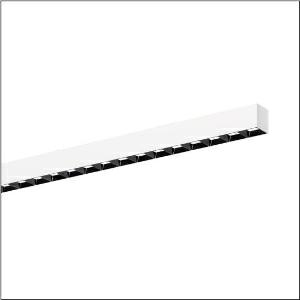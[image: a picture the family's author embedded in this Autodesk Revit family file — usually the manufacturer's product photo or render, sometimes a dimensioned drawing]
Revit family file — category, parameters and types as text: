
# Revit family: silica_r__21_51mx22da34wb_da43
name_source: partatom
category: Lighting Fixtures
units: mm (PartAtom-declared; Revit-internal decimal feet)

## family parameters
Cut with Voids When Loaded = No
Host = Face
Light Source = No
Part Type = Normal
Room Calculation Point = No
Round Connector Dimension = Use Diameter
Shared = No

## types (1)
- --- (1 x LED, 4320 lm, 27.4 W, 3000K)
    Apparent Load = 27 VA
    CIE Flux Codes = 86 100 100 100 100
    Color Rendering = 80
    Color Temperature = 3000K
    Default Elevation = 1800 mm
    Description = Silica® 21, office luminaire, primary light control with darklight reflector, of PMMA, black, CAT 2 (L<= 3000cd/m²), light emission: direct distribution, primary light characteristic: symmetric, installation type: surface-mounted, LED, rated luminous flux: 4.320lm, luminous efficacy: 158lm/W, light colour: 830, colour temperature: 3000K, with terminal, 3+2-pole, max. 2.5mm², mains connection: 220..240V, AC, 50/60Hz, rated input power: 27.4W, luminaire housing, of aluminium, traffic white (RAL 9016), length: 1.204mm, width: 53mm, height: 53mm, protection rating (complete): IP20, insulation class (complete): insulation class I (protective earthing), certification: CE, permissible operating ambient temperature: 0..+35°C, standard: EN 50419, packaging unit: 1 piece
    Height = 0 mm  [stored 0 ft]
    Lamp = 1 x LED
    Lamp Light Flux = 4320 lm
    Lamp Power = 27.4 W
    Lamp count = 1
    Length = 1204 mm
    Luminous efficacy = 158 lm/W
    Manufacturer = Siteco
    ModVariant = No
    Model = 51MX22DA34WB
    Mounting Place = Ceiling
    Mounting Type = Recessed
    Number of Poles = 1
    OnlyDefault = Yes
    Power Factor = 1
    Product Name = Silica® 21
    Product group = office luminaire | ceiling recessed
    ProductGroupID = 401
    Protection Class = Protection class I
    Protection Degree = IP 20
    RLX_Detail_Level = 1
    RLX_Emergency_Light_Flux = 0 lm
    RLX_Emergency_Type = 0
    RLX_Emergency_Type_DB = No
    RlxData = <blob elided: 41077 chars, md5=614700b5>
    Socket = socket
    Standby Power = 0 W
    System Light Flux = 4320 lm
    System Power = 27 W
    Type Comments = factory setting: luminous flux: 100 % | dim-lin: 254 | 392 mA
    Type Image = l_1297779.jpg
    URL = http://relux.com
    VarID = @adj_056459
    Voltage = 0 V
    Weight = 0.00 kg
    Width = 53 mm

note: [stored X ft] marks values corroborated as IEEE doubles in the binary element streams (Revit-internal decimal feet)

## geometry (parser evidence)
native form markers: Blend x4, Sweep x10
no freeform markers — native parametric forms only
